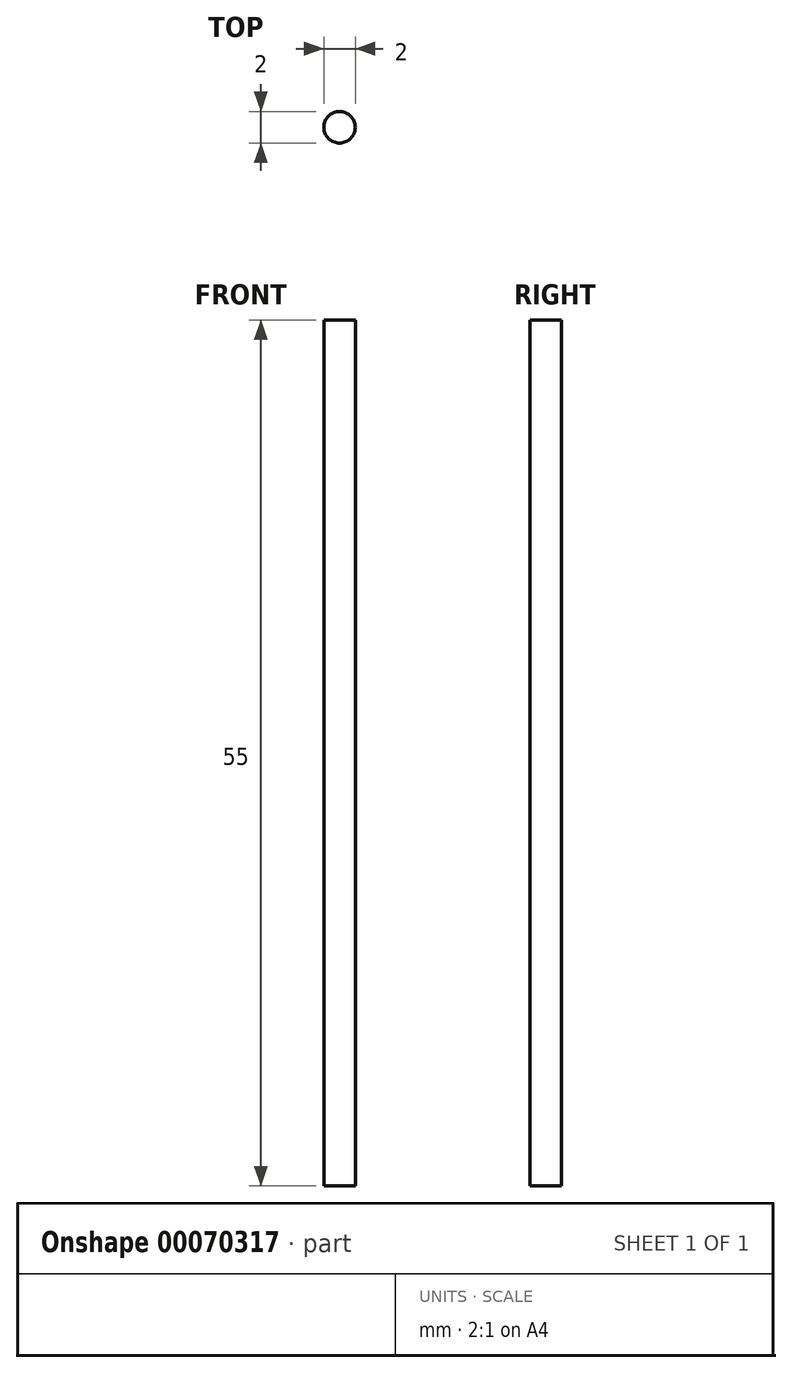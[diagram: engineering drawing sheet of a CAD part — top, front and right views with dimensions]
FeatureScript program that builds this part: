
annotation { "Feature Type Name" : "Feature", "Feature Type Description" : "" }
export const myFeature = defineFeature(function(context is Context, id is Id, definition is map)
    precondition{}
    {
        {
            var Q0;
            Q0=qCreatedBy(makeId("Top.planeOp"),FACE);
            var sketch = newSketch(context, id + "F0", { "sketchPlane" : qUnion([Q0])});
            skCircle(sketch, "E0", {"center": v(0, 0) * mm, "radius": 1 * mm});
            skSolve(sketch);
        }
        {
            var Q0;
            Q0=makeQuery(id+"F0.imprint","IMPRINT",FACE,{"disambiguationData":[TD([[makeQuery(id+"F0.imprint","IMPRINT",EDGE,{"derivedFrom":sQuery(id+"F0.wireOp",EDGE,"E0")}),1.0]])]});
            extrude(context, id + "F1", {"entities" : qUnion([Q0]), "depth" : 55 * mm});
        }
    });
